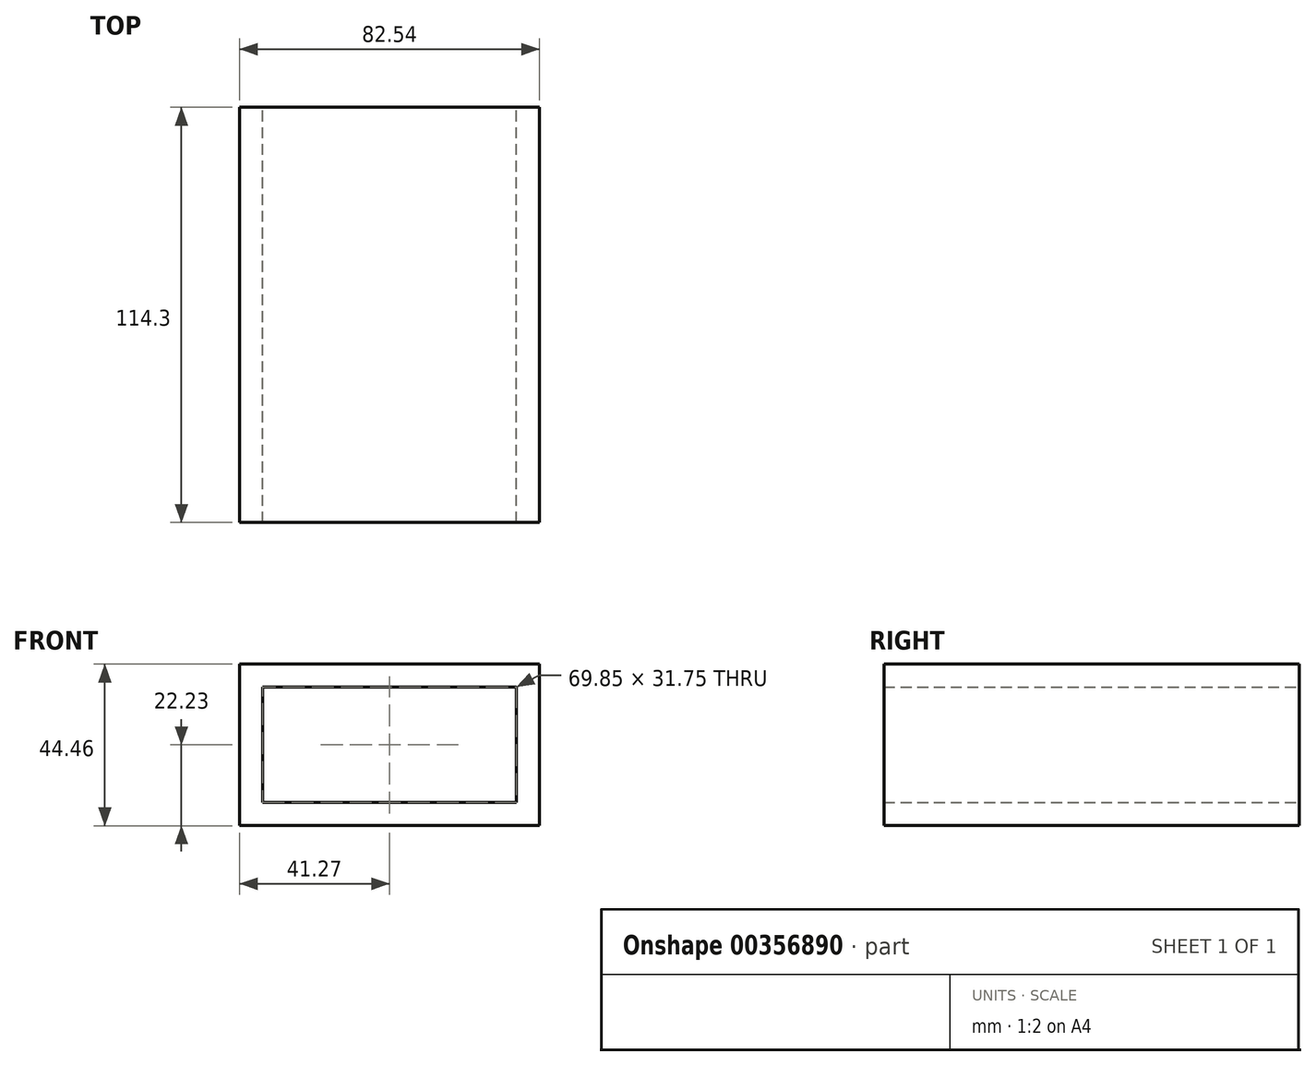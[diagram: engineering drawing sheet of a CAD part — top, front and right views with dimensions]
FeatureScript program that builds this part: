
annotation { "Feature Type Name" : "Feature", "Feature Type Description" : "" }
export const myFeature = defineFeature(function(context is Context, id is Id, definition is map)
    precondition{}
    {
        {
            var Q0;
            Q0=qCreatedBy(makeId("Front.planeOp"),FACE);
            var sketch = newSketch(context, id + "F0", { "sketchPlane" : qUnion([Q0])});
            skLineSegment(sketch, "E0.bottom", {"start": v(34.92, 15.88) * mm, "end": v(-34.93, 15.88) * mm});
            skLineSegment(sketch, "E0.top", {"start": v(34.93, -15.88) * mm, "end": v(-34.93, -15.88) * mm});
            skLineSegment(sketch, "E0.left", {"start": v(34.92, 15.88) * mm, "end": v(34.93, -15.88) * mm});
            skLineSegment(sketch, "E0.right", {"start": v(-34.93, 15.88) * mm, "end": v(-34.92, -15.88) * mm});
            skPoint(sketch, "E0.middle", {"position": v(0, 0) * mm});
            skLineSegment(sketch, "E1.0", {"start": v(41.27, 22.23) * mm, "end": v(-41.28, 22.23) * mm});
            skLineSegment(sketch, "E1.1", {"start": v(41.27, 22.23) * mm, "end": v(41.28, -22.23) * mm});
            skLineSegment(sketch, "E1.2", {"start": v(41.28, -22.23) * mm, "end": v(-41.27, -22.23) * mm});
            skLineSegment(sketch, "E1.3", {"start": v(-41.28, 22.23) * mm, "end": v(-41.27, -22.23) * mm});
            skSolve(sketch);
        }
        {
            var Q0;
            Q0=makeQuery(id+"F0.imprint","IMPRINT",FACE,{"disambiguationData":[TD([[makeQuery(id+"F0.imprint","IMPRINT",EDGE,{"derivedFrom":sQuery(id+"F0.wireOp",EDGE,"E0.bottom")}),-1.0]])]});
            extrude(context, id + "F1", {"entities" : qUnion([Q0]), "depth" : 114.3 * mm});
        }
    });
